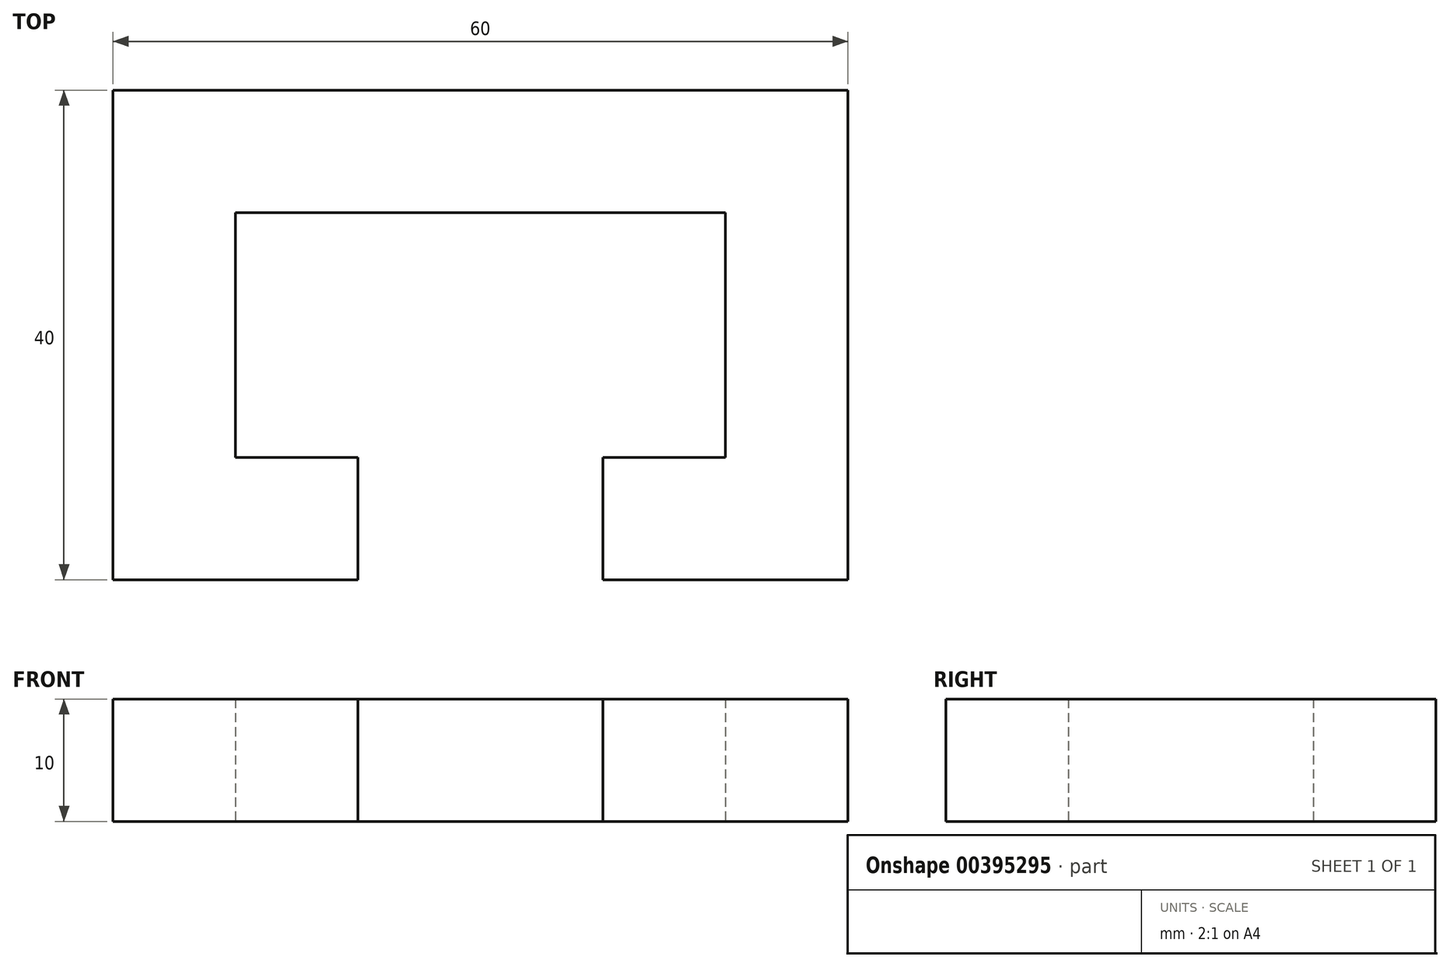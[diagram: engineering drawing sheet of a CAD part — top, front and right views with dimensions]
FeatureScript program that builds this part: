
annotation { "Feature Type Name" : "Feature", "Feature Type Description" : "" }
export const myFeature = defineFeature(function(context is Context, id is Id, definition is map)
    precondition{}
    {
        {
            var Q0;
            Q0=qCreatedBy(makeId("Top.planeOp"),FACE);
            var sketch = newSketch(context, id + "F0", { "sketchPlane" : qUnion([Q0])});
            skLineSegment(sketch, "E0.bottom", {"start": v(-30, 20) * mm, "end": v(30, 20) * mm});
            skLineSegment(sketch, "E0.top", {"start": v(-30, -20) * mm, "end": v(30, -20) * mm});
            skLineSegment(sketch, "E0.left", {"start": v(-30, 20) * mm, "end": v(-30, -20) * mm});
            skLineSegment(sketch, "E0.right", {"start": v(30, 20) * mm, "end": v(30, -20) * mm});
            skPoint(sketch, "E0.middle", {"position": v(0, 0) * mm});
            skLineSegment(sketch, "E1.bottom", {"start": v(-20, 10) * mm, "end": v(20, 10) * mm});
            skLineSegment(sketch, "E1.top", {"start": v(-20, -10) * mm, "end": v(20, -10) * mm});
            skLineSegment(sketch, "E1.left", {"start": v(-20, 10) * mm, "end": v(-20, -10) * mm});
            skLineSegment(sketch, "E1.right", {"start": v(20, 10) * mm, "end": v(20, -10) * mm});
            skLineSegment(sketch, "E2", {"start": v(-20, -10) * mm, "end": v(-10, -10) * mm, "construction": true});
            skLineSegment(sketch, "E3", {"start": v(-10, -10) * mm, "end": v(10, -10) * mm, "construction": true});
            skLineSegment(sketch, "E4", {"start": v(-10, -10) * mm, "end": v(-10, -20) * mm});
            skLineSegment(sketch, "E5", {"start": v(10, -10) * mm, "end": v(10, -20) * mm});
            skSolve(sketch);
        }
        {
            var Q0;
            Q0=makeQuery(id+"F0.imprint","IMPRINT",FACE,{"disambiguationData":[TD([[makeQuery(id+"F0.imprint","IMPRINT",EDGE,{"derivedFrom":sQuery(id+"F0.wireOp",EDGE,"E0.bottom")}),-1.0]])]});
            extrude(context, id + "F1", {"entities" : qUnion([Q0]), "depth" : 10 * mm});
        }
    });
